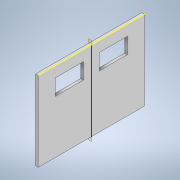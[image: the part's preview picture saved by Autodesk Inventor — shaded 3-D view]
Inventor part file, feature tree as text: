
AUTODESK INVENTOR PART (.ipt)
format: ipt  version: 2020 (Build 240168000, 168)  size: 115,712 bytes
history: native  units: mm
features: sketch x3, extrude x2, plane x1, mirror x1
ambient origin geometry x8: Origin, YZ Plane, XZ Plane, XY Plane, X Axis, Y Axis, Z Axis, Center Point
bodies: Solid1 (feature_tree)
feature tree (7):
  extrude  "Extrusion1"  Depth=2000.0mm
  sketch  "Sketch2"  dims[d2=1500.0mm d3=0.0mm d4=530.0mm]
  extrude  "Extrusion2"  Depth=530.0mm
  plane  "Work Plane1"
  mirror  "Mirror1"
  sketch  "Sketch1"  dims[d0=50.0mm d1=2000.0mm]
  sketch  "Sketch3"  dims[d5=300.0mm d6=320.0mm d7=150.0mm d8=1000.0mm d9=0.0mm d10=0.0mm]
